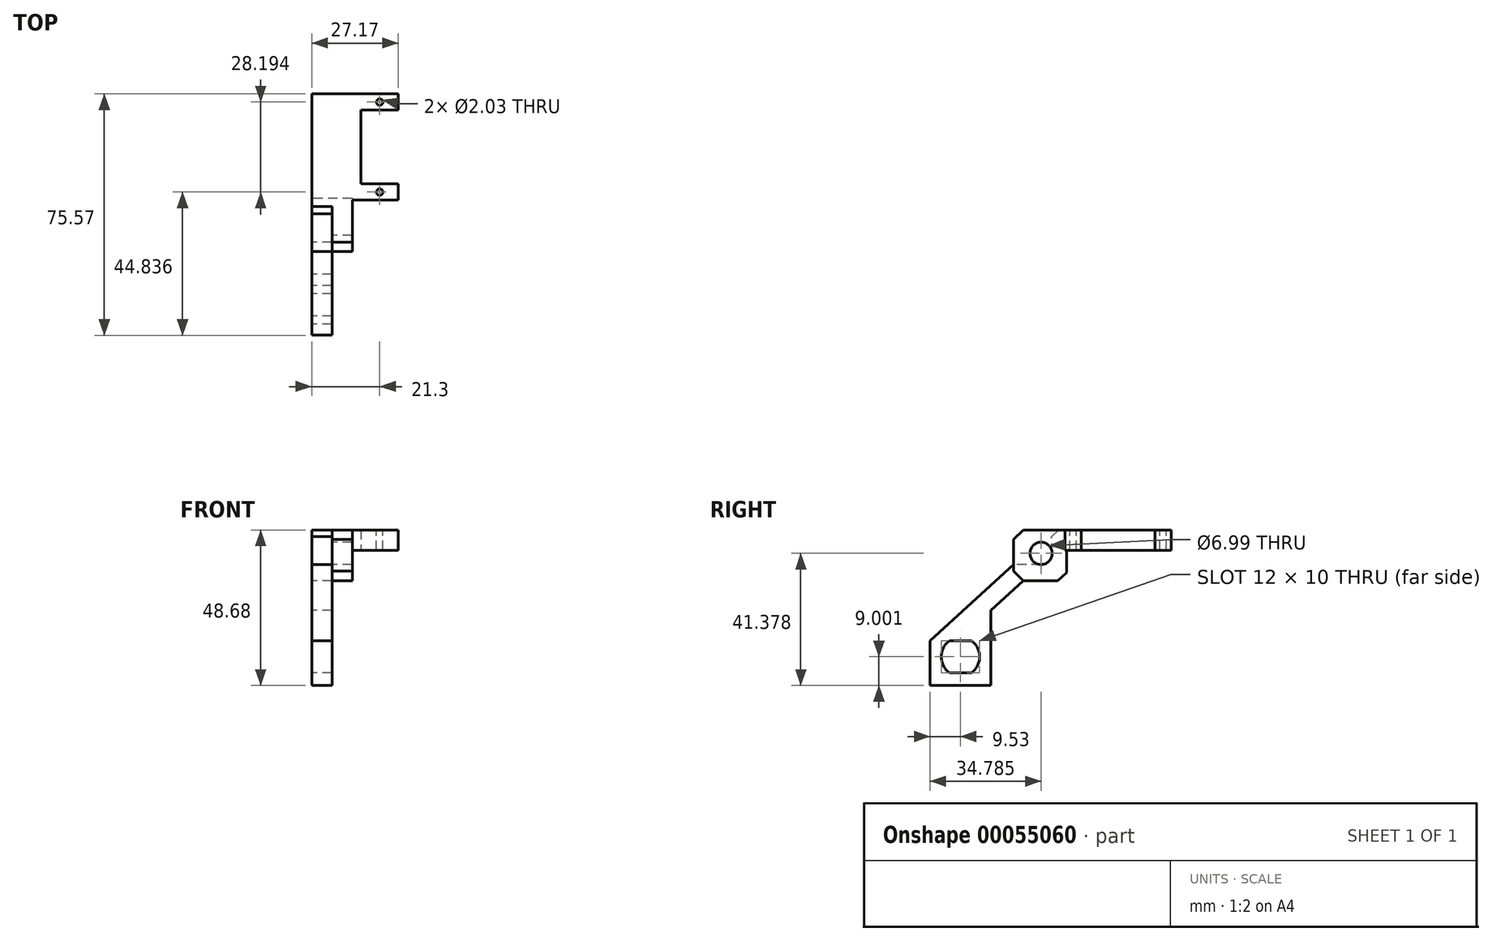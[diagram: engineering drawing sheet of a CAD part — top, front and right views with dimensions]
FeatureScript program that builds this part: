
annotation { "Feature Type Name" : "Feature", "Feature Type Description" : "" }
export const myFeature = defineFeature(function(context is Context, id is Id, definition is map)
    precondition{}
    {
        {
            var Q0;
            Q0=qCreatedBy(makeId("Right.planeOp"),FACE);
            var sketch = newSketch(context, id + "F0", { "sketchPlane" : qUnion([Q0])});
            skLineSegment(sketch, "E0", {"start": v(0, 0) * mm, "end": v(-32.77, 0) * mm});
            skLineSegment(sketch, "E1", {"start": v(-32.77, 0) * mm, "end": v(-37.48, 0) * mm, "construction": true});
            skLineSegment(sketch, "E2", {"start": v(-37.48, 0) * mm, "end": v(-49.34, -10.8) * mm, "construction": true});
            skLineSegment(sketch, "E3", {"start": v(-49.34, -10.8) * mm, "end": v(-75.57, -34.68) * mm});
            skLineSegment(sketch, "E4", {"start": v(-75.57, -34.68) * mm, "end": v(-75.57, -48.68) * mm});
            skLineSegment(sketch, "E5", {"start": v(-75.57, -48.68) * mm, "end": v(-56.52, -48.68) * mm});
            skLineSegment(sketch, "E6", {"start": v(-56.52, -48.68) * mm, "end": v(-56.52, -25.12) * mm});
            skLineSegment(sketch, "E7", {"start": v(-56.52, -25.12) * mm, "end": v(-46.36, -15.87) * mm});
            skLineSegment(sketch, "E8", {"start": v(-32.77, -6.35) * mm, "end": v(0, -6.35) * mm});
            skLineSegment(sketch, "E9", {"start": v(0, -6.35) * mm, "end": v(0, 0) * mm});
            skLineSegment(sketch, "E10", {"start": v(-4.83, 0) * mm, "end": v(-4.83, -6.35) * mm, "construction": true});
            skLineSegment(sketch, "E11", {"start": v(-27.94, 0) * mm, "end": v(-27.94, -6.35) * mm, "construction": true});
            skPoint(sketch, "E12", {"position": v(-66.04, -48.68) * mm});
            skLineSegment(sketch, "E13", {"start": v(-72.04, -34.68) * mm, "end": v(-69.54, -34.68) * mm, "construction": true});
            skLineSegment(sketch, "E14", {"start": v(-69.54, -34.68) * mm, "end": v(-62.54, -34.68) * mm});
            skLineSegment(sketch, "E15", {"start": v(-62.54, -34.68) * mm, "end": v(-60.04, -34.68) * mm, "construction": true});
            skLineSegment(sketch, "E16", {"start": v(-60.04, -34.68) * mm, "end": v(-60.04, -44.68) * mm, "construction": true});
            skLineSegment(sketch, "E17", {"start": v(-60.04, -44.68) * mm, "end": v(-62.54, -44.68) * mm, "construction": true});
            skLineSegment(sketch, "E18", {"start": v(-62.54, -44.68) * mm, "end": v(-69.54, -44.68) * mm});
            skLineSegment(sketch, "E19", {"start": v(-69.54, -44.68) * mm, "end": v(-72.04, -44.68) * mm, "construction": true});
            skLineSegment(sketch, "E20", {"start": v(-72.04, -44.68) * mm, "end": v(-72.04, -34.68) * mm, "construction": true});
            skArc(sketch, "E21", {"start": v(-62.54, -44.68) * mm, "mid": v(-60.04, -39.68) * mm, "end": v(-62.54, -34.68) * mm});
            skArc(sketch, "E22", {"start": v(-69.54, -34.68) * mm, "mid": v(-72.04, -39.68) * mm, "end": v(-69.54, -44.68) * mm});
            skPoint(sketch, "E23", {"position": v(-66.04, -44.68) * mm});
            skCircle(sketch, "E24", {"center": v(-40.79, -7.3) * mm, "radius": 3.18 * mm, "construction": true});
            skPoint(sketch, "E25", {"position": v(-42.92, -4.95) * mm});
            skLineSegment(sketch, "E26", {"start": v(-37.3, -7.18) * mm, "end": v(-37.48, -2.06) * mm});
            skLineSegment(sketch, "E27", {"start": v(-40.79, -10.8) * mm, "end": v(-49.34, -10.8) * mm});
            skLineSegment(sketch, "E28", {"start": v(-32.77, -6.35) * mm, "end": v(-32.77, -13.31) * mm});
            skLineSegment(sketch, "E29", {"start": v(-32.77, -13.31) * mm, "end": v(-35.58, -15.87) * mm});
            skLineSegment(sketch, "E30", {"start": v(-35.58, -15.87) * mm, "end": v(-46.36, -15.87) * mm});
            skArc(sketch, "E31", {"start": v(-40.79, -10.8) * mm, "mid": v(-38.27, -9.73) * mm, "end": v(-37.3, -7.18) * mm});
            skLineSegment(sketch, "E32", {"start": v(-40.79, -7.3) * mm, "end": v(-32.77, 0) * mm, "construction": true});
            skLineSegment(sketch, "E33", {"start": v(-37.48, -2.06) * mm, "end": v(-35.22, 0) * mm});
            skLineSegment(sketch, "E34", {"start": v(-35.22, 0) * mm, "end": v(-32.77, 0) * mm});
            skSolve(sketch);
        }
        {
            var Q0;
            Q0 = qSketchRegion(id + "F0", true);
            extrude(context, id + "F1", {"entities" : qUnion([Q0]), "depth" : 6.35 * mm});
        }
        {
            var Q0;
            {var subQ0=sQuery(id+"F0.wireOp",EDGE,"E28");var subQ1=sQuery(id+"F0.wireOp",EDGE,"E8");var subQ2=sQuery(id+"F0.wireOp",EDGE,"E3");var subQ3=sQuery(id+"F0.wireOp",EDGE,"E27");var subQ4=sQuery(id+"F0.wireOp",EDGE,"E26");var subQ5=sQuery(id+"F0.wireOp",EDGE,"E5");var subQ6=sQuery(id+"F0.wireOp",EDGE,"E21");var subQ7=sQuery(id+"F0.wireOp",EDGE,"E33");var subQ8=sQuery(id+"F0.wireOp",EDGE,"E4");var subQ9=sQuery(id+"F0.wireOp",EDGE,"E29");var subQ10=sQuery(id+"F0.wireOp",EDGE,"E31");var subQ11=sQuery(id+"F0.wireOp",EDGE,"E14");var subQ12=sQuery(id+"F0.wireOp",EDGE,"E30");var subQ13=sQuery(id+"F0.wireOp",EDGE,"E22");var subQ14=sQuery(id+"F0.wireOp",EDGE,"E34");var subQ15=sQuery(id+"F0.wireOp",EDGE,"E0");var subQ16=sQuery(id+"F0.wireOp",EDGE,"E6");var subQ17=sQuery(id+"F0.wireOp",EDGE,"E7");var subQ18=sQuery(id+"F0.wireOp",EDGE,"E18");Q0=makeQuery(id+"FeyVyrOEcjYHzYY_1.boolean.opBoolean","SPLIT",FACE,{"disambiguationData":[TD([makeQuery(id+"F1.opExtrude","SWEPT_FACE",FACE,{"disambiguationData":[OSD([subQ2])]})])],"derivedFrom":makeQuery(id+"F1.opExtrude","CAP_FACE",FACE,{"disambiguationData":[OSD([subQ15,subQ2,subQ8,subQ5,subQ16,subQ17,subQ1,sQuery(id+"F0.wireOp",EDGE,"E9"),subQ11,subQ18,subQ6,subQ13,subQ4,subQ3,subQ0,subQ9,subQ12,subQ10,subQ7,subQ14])],"isStart":false})});}
            var sketch = newSketch(context, id + "F2", { "sketchPlane" : qUnion([Q0])});
            skCircle(sketch, "E35", {"center": v(-40.79, -7.3) * mm, "radius": 3.5 * mm});
            skLineSegment(sketch, "E36", {"start": v(-32.77, 0) * mm, "end": v(-46.36, 0) * mm});
            skLineSegment(sketch, "E37", {"start": v(-46.36, 0) * mm, "end": v(-49.36, -3) * mm});
            skLineSegment(sketch, "E38", {"start": v(-49.36, -3) * mm, "end": v(-49.36, -12.88) * mm});
            skLineSegment(sketch, "E39", {"start": v(-49.36, -12.88) * mm, "end": v(-46.36, -15.87) * mm});
            skLineSegment(sketch, "E40", {"start": v(-46.36, -15.87) * mm, "end": v(-35.58, -15.87) * mm});
            skLineSegment(sketch, "E41", {"start": v(-35.58, -15.87) * mm, "end": v(-32.77, -13.31) * mm});
            skLineSegment(sketch, "E42", {"start": v(-32.77, -13.31) * mm, "end": v(-32.77, 0) * mm});
            skSolve(sketch);
        }
        {
            var Q0;
            Q0 = qSketchRegion(id + "F2", true);
            extrude(context, id + "F3", {"entities" : qUnion([Q0]), "operationType" : NewBodyOperationType.ADD, "depth" : 6.35 * mm});
        }
        {
            var Q0;
            {var subQ0=sQuery(id+"F0.wireOp",EDGE,"E28");var subQ1=sQuery(id+"F0.wireOp",EDGE,"E9");var subQ2=sQuery(id+"F0.wireOp",EDGE,"E8");var subQ3=sQuery(id+"F0.wireOp",EDGE,"E34");var subQ4=sQuery(id+"F0.wireOp",EDGE,"E0");Q0=makeQuery(id+"F3.boolean.opBoolean","SPLIT",FACE,{"disambiguationData":[TD([makeQuery(id+"F1.opExtrude","SWEPT_FACE",FACE,{"disambiguationData":[OSD([subQ2])]})])],"derivedFrom":makeQuery(id+"F1.opExtrude","CAP_FACE",FACE,{"disambiguationData":[OSD([subQ4,sQuery(id+"F0.wireOp",EDGE,"E3"),sQuery(id+"F0.wireOp",EDGE,"E4"),sQuery(id+"F0.wireOp",EDGE,"E5"),sQuery(id+"F0.wireOp",EDGE,"E6"),sQuery(id+"F0.wireOp",EDGE,"E7"),subQ2,subQ1,sQuery(id+"F0.wireOp",EDGE,"E14"),sQuery(id+"F0.wireOp",EDGE,"E18"),sQuery(id+"F0.wireOp",EDGE,"E21"),sQuery(id+"F0.wireOp",EDGE,"E22"),sQuery(id+"F0.wireOp",EDGE,"E26"),sQuery(id+"F0.wireOp",EDGE,"E27"),subQ0,sQuery(id+"F0.wireOp",EDGE,"E29"),sQuery(id+"F0.wireOp",EDGE,"E30"),sQuery(id+"F0.wireOp",EDGE,"E31"),sQuery(id+"F0.wireOp",EDGE,"E33"),subQ3])],"isStart":false})});}
            var sketch = newSketch(context, id + "F4", { "sketchPlane" : qUnion([Q0])});
            skLineSegment(sketch, "E43.bottom", {"start": v(0, 0) * mm, "end": v(-33.27, 0) * mm});
            skLineSegment(sketch, "E43.top", {"start": v(0, -6.35) * mm, "end": v(-33.27, -6.35) * mm});
            skLineSegment(sketch, "E43.left", {"start": v(0, 0) * mm, "end": v(0, -6.35) * mm});
            skLineSegment(sketch, "E43.right", {"start": v(-33.27, 0) * mm, "end": v(-33.27, -6.35) * mm});
            skSolve(sketch);
        }
        {
            var Q0;
            Q0 = qSketchRegion(id + "F4", true);
            extrude(context, id + "F5", {"entities" : qUnion([Q0]), "operationType" : NewBodyOperationType.ADD, "depth" : 9.08 * mm});
        }
        {
            var Q0;
            Q0=makeQuery(id+"F5.opExtrude","CAP_FACE",FACE,{"disambiguationData":[OSD([sQuery(id+"F4.wireOp",EDGE,"E43.bottom"),sQuery(id+"F4.wireOp",EDGE,"E43.top"),sQuery(id+"F4.wireOp",EDGE,"E43.left"),sQuery(id+"F4.wireOp",EDGE,"E43.right")])],"isStart":false});
            var sketch = newSketch(context, id + "F6", { "sketchPlane" : qUnion([Q0])});
            skLineSegment(sketch, "E44.bottom", {"start": v(0, 0) * mm, "end": v(-5.08, 0) * mm});
            skLineSegment(sketch, "E44.top", {"start": v(0, -6.35) * mm, "end": v(-5.08, -6.35) * mm});
            skLineSegment(sketch, "E44.left", {"start": v(0, 0) * mm, "end": v(0, -6.35) * mm});
            skLineSegment(sketch, "E44.right", {"start": v(-5.08, 0) * mm, "end": v(-5.08, -6.35) * mm});
            skLineSegment(sketch, "E45.bottom", {"start": v(-28.2, 0) * mm, "end": v(-33.27, 0) * mm});
            skLineSegment(sketch, "E45.top", {"start": v(-28.2, -6.35) * mm, "end": v(-33.27, -6.35) * mm});
            skLineSegment(sketch, "E45.left", {"start": v(-28.2, 0) * mm, "end": v(-28.2, -6.35) * mm});
            skLineSegment(sketch, "E45.right", {"start": v(-33.27, 0) * mm, "end": v(-33.27, -6.35) * mm});
            skSolve(sketch);
        }
        {
            var Q0;
            Q0 = qSketchRegion(id + "F6", true);
            extrude(context, id + "F7", {"entities" : qUnion([Q0]), "operationType" : NewBodyOperationType.ADD, "depth" : 11.73 * mm});
        }
        {
            var Q0;
            Q0=makeQuery(id+"F7.boolean.opBoolean","MERGE",FACE,{"derivedFrom":[makeQuery(id+"F5.boolean.opBoolean","MERGE",FACE,{"derivedFrom":[makeQuery(id+"F3.boolean.opBoolean","MERGE",FACE,{"derivedFrom":[makeQuery(id+"F1.opExtrude","SWEPT_FACE",FACE,{"disambiguationData":[OSD([sQuery(id+"F0.wireOp",EDGE,"E0"),sQuery(id+"F0.wireOp",EDGE,"E34")])]}),makeQuery(id+"F3.opExtrude","SWEPT_FACE",FACE,{"disambiguationData":[OSD([sQuery(id+"F2.wireOp",EDGE,"E36")])]})]}),makeQuery(id+"F5.opExtrude","SWEPT_FACE",FACE,{"disambiguationData":[OSD([sQuery(id+"F4.wireOp",EDGE,"E43.bottom")])]})]}),makeQuery(id+"F7.opExtrude","SWEPT_FACE",FACE,{"disambiguationData":[OSD([sQuery(id+"F6.wireOp",EDGE,"E44.bottom")])]}),makeQuery(id+"F7.opExtrude","SWEPT_FACE",FACE,{"disambiguationData":[OSD([sQuery(id+"F6.wireOp",EDGE,"E45.bottom")])]})]});
            var sketch = newSketch(context, id + "F8", { "sketchPlane" : qUnion([Q0])});
            skCircle(sketch, "E46", {"center": v(21.3, -30.73) * mm, "radius": 1.02 * mm});
            skCircle(sketch, "E47", {"center": v(21.3, -2.54) * mm, "radius": 1.02 * mm});
            skPoint(sketch, "E48", {"position": v(27.17, -2.54) * mm});
            skPoint(sketch, "E49", {"position": v(21.3, -5.08) * mm});
            skPoint(sketch, "E50", {"position": v(27.17, -30.73) * mm});
            skSolve(sketch);
        }
        {
            var Q0;
            Q0 = qSketchRegion(id + "F8", true);
            extrude(context, id + "F9", {"entities" : qUnion([Q0]), "operationType" : NewBodyOperationType.REMOVE, "endBound" : BoundingType.UP_TO_NEXT, "oppositeDirection" : true, "depth" : 25.4 * mm});
        }
    });
